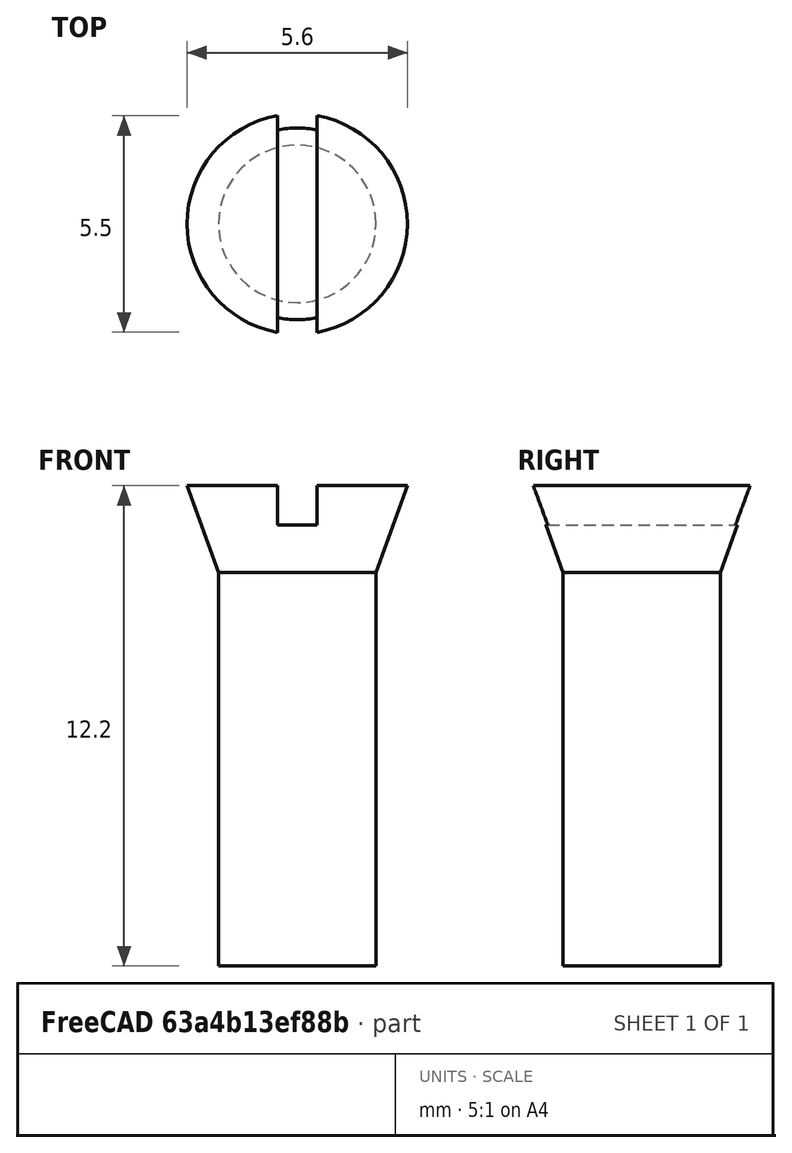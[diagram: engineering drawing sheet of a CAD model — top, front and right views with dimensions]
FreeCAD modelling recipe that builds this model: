
FCSTD DOCUMENT  (FreeCAD 0.18.4R)
Label: tutorial_freecad_ex14_b
License: All rights reserved
LicenseURL: http://en.wikipedia.org/wiki/All_rights_reserved
objects: Part::Cylinder×1, Part::Cone×1, Part::Box×1, Part::Cut×1, Part::MultiFuse×1
note: 5 computed .brp shape members not serialized (recipe doc carries the construction recipe); baked Part::Feature solids carry a one-line shape summary decoded from their .brp

FEATURE [Part::Cylinder] Cylinder  label="cuerpo"
  Angle = 360
  AttacherType = Attacher::AttachEngine3D
  Height = 10
  Radius = 2
FEATURE [Part::Cone] Cone  label="cabeza"
  Angle = 360
  AttacherType = Attacher::AttachEngine3D
  Height = 2.2
  Placement = pos=(0,0,10) rot=(0,0,1;0rad)
  Radius1 = 2
  Radius2 = 2.8
FEATURE [Part::Box] Box  label="ranura_destornillador"
  AttacherType = Attacher::AttachEngine3D
  Height = 2
  Length = 1
  Placement = pos=(-0.5,-3,11.2) rot=(0,0,1;0rad)
  Width = 6
FEATURE [Part::Cut] Cut  label="cabeza_final"
  Base = -> Cone
  Refine = true
  Tool = -> Box
FEATURE [Part::MultiFuse] Fusion  label="tornillo_sin_rosca"
  Refine = true
  Shapes = -> [Cylinder,Cut]
